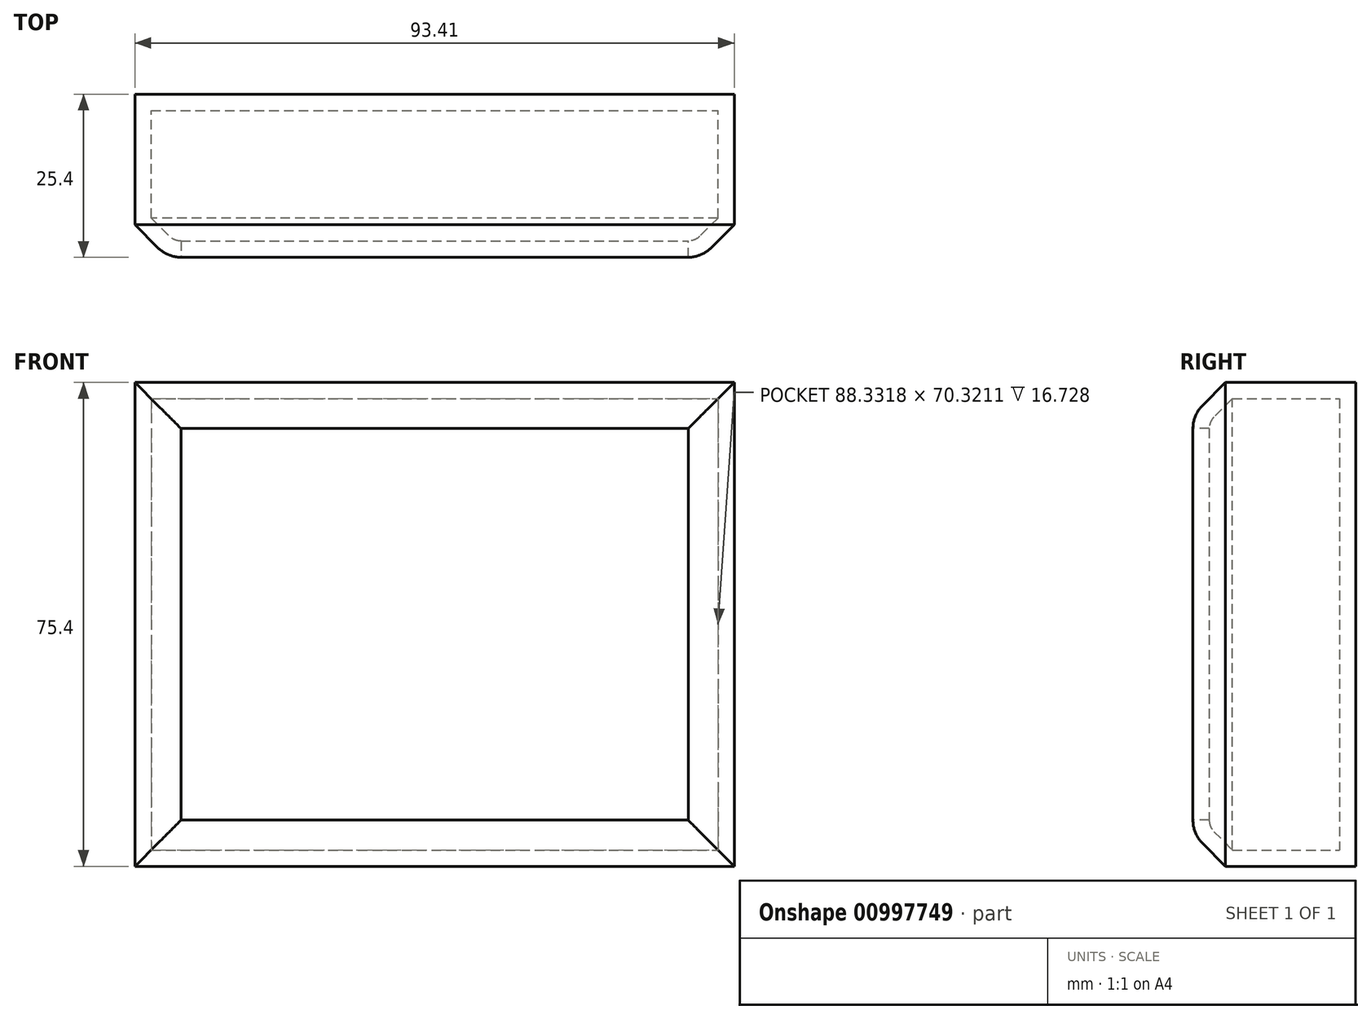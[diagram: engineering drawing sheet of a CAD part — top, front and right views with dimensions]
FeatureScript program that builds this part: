
annotation { "Feature Type Name" : "Feature", "Feature Type Description" : "" }
export const myFeature = defineFeature(function(context is Context, id is Id, definition is map)
    precondition{}
    {
        {
            var Q0;
            Q0=qCreatedBy(makeId("Front.planeOp"),FACE);
            var sketch = newSketch(context, id + "F0", { "sketchPlane" : qUnion([Q0])});
            skLineSegment(sketch, "E0.bottom", {"start": v(-46.25, 34.34) * mm, "end": v(47.16, 34.34) * mm});
            skLineSegment(sketch, "E0.top", {"start": v(-46.25, -41.06) * mm, "end": v(47.16, -41.06) * mm});
            skLineSegment(sketch, "E0.left", {"start": v(-46.25, 34.34) * mm, "end": v(-46.25, -41.06) * mm});
            skLineSegment(sketch, "E0.right", {"start": v(47.16, 34.34) * mm, "end": v(47.16, -41.06) * mm});
            skSolve(sketch);
        }
        {
            var Q0;
            Q0 = qSketchRegion(id + "F0", true);
            extrude(context, id + "F1", {"entities" : qUnion([Q0]), "depth" : 25.4 * mm, "offsetDistance" : 25.4 * mm});
        }
        {
            var Q0;
            Q0=makeQuery(id+"F1.opExtrude","CAP_FACE",FACE,{"disambiguationData":[OSD([sQuery(id+"F0.wireOp",EDGE,"E0.bottom"),sQuery(id+"F0.wireOp",EDGE,"E0.top"),sQuery(id+"F0.wireOp",EDGE,"E0.left"),sQuery(id+"F0.wireOp",EDGE,"E0.right")])],"isStart":false});
            chamfer(context, id + "F2", {"entities" : qUnion([Q0]), "width" : 5.08 * mm, "tangentPropagation" : true});
        }
        {
            var Q0;
            Q0=makeQuery(id+"F1.opExtrude","CAP_FACE",FACE,{"disambiguationData":[OSD([sQuery(id+"F0.wireOp",EDGE,"E0.bottom"),sQuery(id+"F0.wireOp",EDGE,"E0.top"),sQuery(id+"F0.wireOp",EDGE,"E0.left"),sQuery(id+"F0.wireOp",EDGE,"E0.right")])],"isStart":false});
            fillet(context, id + "F3", {"entities" : qUnion([Q0]), "radius" : 5.08 * mm, "tangentPropagation" : true, "allowEdgeOverflow" : false});
        }
        {
            var Q0;
            Q0=makeQuery(id+"F1.opExtrude","CAP_FACE",FACE,{"disambiguationData":[OSD([sQuery(id+"F0.wireOp",EDGE,"E0.bottom"),sQuery(id+"F0.wireOp",EDGE,"E0.top"),sQuery(id+"F0.wireOp",EDGE,"E0.left"),sQuery(id+"F0.wireOp",EDGE,"E0.right")])],"isStart":false});
            shell(context, id + "F4", {"entities" : qUnion([Q0]), "thickness" : 2.54 * mm});
        }
    });
